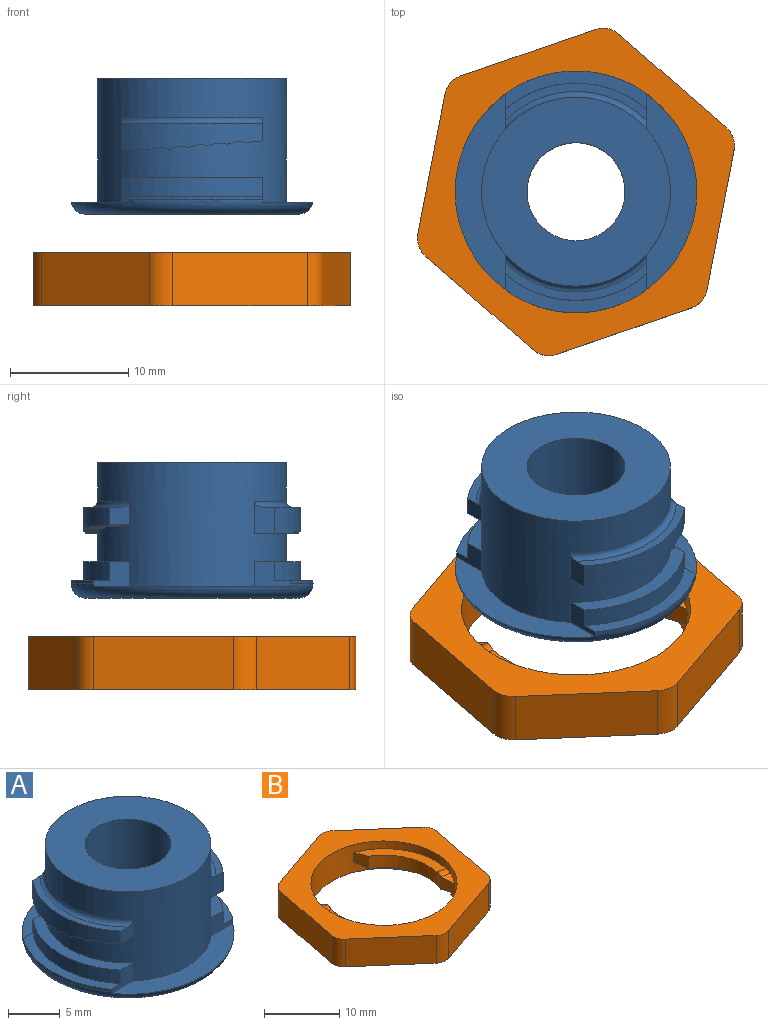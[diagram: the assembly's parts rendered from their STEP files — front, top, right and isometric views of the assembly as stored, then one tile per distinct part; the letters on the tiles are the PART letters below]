
ASSEMBLY  parts=2 mates=1
PART A: 51 faces, bbox 22.2x22.2x11.5 mm
  f0: plane 12x3.28mm, normal (0,0,1), area 13.6mm2, adj f1,f5,f6,f42
  f1: cylinder r=10.25mm len=12mm, axis (0,0,-1), area 3.8mm2, adj f0,f2,f5,f6
  f2: torus R=9.05mm, axis (0,0,-1), area 108.5mm2, adj f1,f3,f4,f5,f6,f37,f38,f49
  f3: plane 3.03x2.11mm, normal (0,1,0), area 4.2mm2, adj f2,f35,f36,f37,f43,f44,f50
  f4: plane 3.03x2.11mm, normal (0,-1,0), area 4.2mm2, adj f2,f35,f36,f37,f43,f44,f49
  f5: plane 3.03x2.11mm, normal (0,-1,0), area 4.2mm2, adj f0,f1,f2,f35,f42,f45,f49
  f6: plane 3.03x2.11mm, normal (0,1,0), area 4.2mm2, adj f0,f1,f2,f35,f42,f45,f50
  f7: plane 2.7x1.68mm, normal (0,1,0), area 3.8mm2, adj f8,f32,f35,f40,f46
  f8: plane 3.22x2.5mm, normal (0,0,-1), area 3.7mm2, adj f7,f34,f35,f40
  f9: plane 2.7x1.68mm, normal (0,-1,0), area 3.8mm2, adj f10,f20,f35,f41,f47
  f10: plane 3.22x2.5mm, normal (0,0,-1), area 3.7mm2, adj f9,f22,f35,f41
  f11: plane 2.7x1.43mm, normal (0,0.09,-1), area 2.2mm2, adj f12,f21,f35,f41
  f12: cylinder r=1.95mm len=2.11mm, axis (1,0,0), area 2mm2, adj f11,f13,f35,f41
  f13: plane 1.34x0.15mm, normal (0,0.09,-1), area 0.2mm2, adj f12,f14,f35,f41
  f14: cylinder r=1.95mm len=1.64mm, axis (1,0,0), area 1.9mm2, adj f13,f15,f35,f41
  f15: plane 1.24x0.15mm, normal (0,0.09,-1), area 0.2mm2, adj f14,f16,f35,f41
  f16: cylinder r=1.95mm len=1.49mm, axis (1,0,0), area 1.9mm2, adj f15,f17,f35,f41
  f17: plane 1.21x0.15mm, normal (0,0.09,-1), area 0.2mm2, adj f16,f18,f35,f41
  f18: cylinder r=1.95mm len=1.49mm, axis (1,0,0), area 1.9mm2, adj f17,f19,f35,f41
  f19: plane 1.27x0.15mm, normal (0,0.09,-1), area 0.2mm2, adj f18,f22,f35,f41
  f20: plane 12x3.18mm, normal (0,0,1), area 9.2mm2, adj f9,f21,f41,f47
  f21: plane 2x1.68mm, normal (0,1,0), area 2.6mm2, adj f11,f20,f35,f41,f47
  f22: cylinder r=1.95mm len=1.79mm, axis (1,0,0), area 2mm2, adj f10,f19,f35,f41
  f23: plane 2.7x1.43mm, normal (0,-0.09,-1), area 2.2mm2, adj f24,f33,f35,f40
  f24: cylinder r=1.95mm len=2.11mm, axis (-1,0,0), area 2mm2, adj f23,f25,f35,f40
  f25: plane 1.34x0.15mm, normal (0,-0.09,-1), area 0.2mm2, adj f24,f26,f35,f40
  f26: cylinder r=1.95mm len=1.64mm, axis (-1,0,0), area 1.9mm2, adj f25,f27,f35,f40
  f27: plane 1.24x0.15mm, normal (0,-0.09,-1), area 0.2mm2, adj f26,f28,f35,f40
  f28: cylinder r=1.95mm len=1.49mm, axis (-1,0,0), area 1.8mm2, adj f27,f29,f35,f40
  f29: plane 1.21x0.15mm, normal (0,-0.09,-1), area 0.2mm2, adj f28,f30,f35,f40
  f30: cylinder r=1.95mm len=1.49mm, axis (-1,0,0), area 1.9mm2, adj f29,f31,f35,f40
  f31: plane 1.27x0.15mm, normal (0,-0.09,-1), area 0.2mm2, adj f30,f34,f35,f40
  f32: plane 12x3.18mm, normal (0,0,1), area 9.2mm2, adj f7,f33,f40,f46
  f33: plane 2x1.68mm, normal (0,-1,0), area 2.6mm2, adj f23,f32,f35,f40,f46
  f34: cylinder r=1.95mm len=1.79mm, axis (-1,0,0), area 2mm2, adj f8,f31,f35,f40
  f35: cylinder r=8mm len=16mm, axis (0,0,-1), area 405.6mm2, adj f3,f4,f5,f6,f7,f8,f9,f10
  f36: plane 12x3.28mm, normal (0,0,1), area 13.6mm2, adj f3,f4,f37,f43
  f37: cylinder r=10.25mm len=12mm, axis (0,0,-1), area 3.8mm2, adj f2,f3,f4,f36
  f38: plane 18.1x18.1mm, normal (0,0,-1), area 203.2mm2, adj f2,f39
  f39: cylinder r=4.15mm len=11.5mm, axis (0,0,-1), area 299.9mm2, adj f38,f48
  f40: cylinder r=9.2mm len=12mm, axis (0,0,1), area 24.9mm2, adj f7,f8,f23,f24,f25,f26,f27,f28
  f41: cylinder r=9.2mm len=12mm, axis (0,0,1), area 24.9mm2, adj f9,f10,f11,f12,f13,f14,f15,f16
  f42: cylinder r=9.2mm len=12mm, axis (0,0,1), area 20.9mm2, adj f0,f5,f6,f45
  f43: cylinder r=9.2mm len=12mm, axis (0,0,1), area 20.9mm2, adj f3,f4,f36,f44
  f44: plane 12x3.91mm, normal (0,0,1), area 16mm2, adj f3,f4,f35,f43
  f45: plane 12x3.91mm, normal (0,0,1), area 16mm2, adj f5,f6,f35,f42
  f46: torus R=8.5mm, axis (0,0,-1), area 10.6mm2, adj f7,f32,f33,f35
  f47: torus R=8.5mm, axis (0,0,1), area 10.6mm2, adj f9,f20,f21,f35
  f48: plane 16x16mm, normal (0,0,1), area 147mm2, adj f35,f39
  f49: plane 16.58x4.23mm, normal (0,0,1), area 34.6mm2, adj f2,f4,f5,f35
  f50: plane 16.58x4.23mm, normal (0,0,1), area 34.6mm2, adj f2,f3,f6,f35
PART B: 33 faces, bbox 26.9x27.7x4.5 mm
  f0: cylinder r=1.28mm len=2.03mm, axis (0.66,0.75,0), area 1.9mm2, adj f1,f7,f8,f32
  f1: cylinder r=9.7mm len=19.4mm, axis (0,0,-1), area 207.6mm2, adj f0,f2,f3,f4,f5,f8,f9,f10
  f2: cylinder r=1.28mm len=2.03mm, axis (-0.66,-0.75,0), area 1.9mm2, adj f1,f5,f6,f31
  f3: plane 11.26x6.27mm, normal (0,0,1), area 18.4mm2, adj f1,f6,f11,f29
  f4: plane 11.26x6.27mm, normal (0,0,1), area 18.4mm2, adj f1,f7,f10,f27
  f5: plane 12.58x4.59mm, normal (0,0,-1), area 18.4mm2, adj f1,f2,f6,f9
  f6: cylinder r=8.2mm len=10.15mm, axis (0,0,-1), area 23.6mm2, adj f2,f3,f5,f9,f11,f29,f30
  f7: cylinder r=8.2mm len=10.15mm, axis (0,0,-1), area 23.6mm2, adj f0,f4,f8,f10,f12,f27
  f8: plane 12.58x4.59mm, normal (0,0,-1), area 18.4mm2, adj f0,f1,f7,f12
  f9: plane 2x1.98mm, normal (-0.95,-0.33,0), area 3.7mm2, adj f1,f5,f6,f30
  f10: plane 2x1.98mm, normal (0.95,0.33,0), area 3.7mm2, adj f1,f4,f7,f32
  f11: plane 2x1.98mm, normal (-0.95,-0.33,0), area 3.7mm2, adj f1,f3,f6,f31
  f12: plane 2x1.98mm, normal (0.95,0.33,0), area 3.7mm2, adj f1,f7,f8,f28
  f13: plane 11.43x4.5mm, normal (-0.33,0.95,0), area 54.4mm2, adj f19,f20,f25,f26
  f14: plane 9.13x7.93mm, normal (-0.66,-0.75,0), area 54.4mm2, adj f21,f22,f25,f26
  f15: plane 11.87x4.5mm, normal (0.98,-0.19,0), area 54.4mm2, adj f23,f24,f25,f26
  f16: plane 11.43x4.5mm, normal (0.33,-0.95,0), area 54.4mm2, adj f22,f23,f25,f26
  f17: plane 11.87x4.5mm, normal (-0.98,0.19,0), area 54.4mm2, adj f20,f21,f25,f26
  f18: plane 9.13x7.93mm, normal (0.66,0.75,0), area 54.4mm2, adj f19,f24,f25,f26
  f19: cylinder r=2mm len=4.5mm, axis (0,0,1), area 9.4mm2, adj f13,f18,f25,f26
  f20: cylinder r=2mm len=4.5mm, axis (0,0,1), area 9.4mm2, adj f13,f17,f25,f26
  f21: cylinder r=2mm len=4.5mm, axis (0,0,1), area 9.4mm2, adj f14,f17,f25,f26
  f22: cylinder r=2mm len=4.5mm, axis (0,0,1), area 9.4mm2, adj f14,f16,f25,f26
  f23: cylinder r=2mm len=4.5mm, axis (0,0,1), area 9.4mm2, adj f15,f16,f25,f26
  f24: cylinder r=2mm len=4.5mm, axis (0,0,1), area 9.4mm2, adj f15,f18,f25,f26
  f25: plane 27.74x26.86mm, normal (0,0,1), area 241.9mm2, adj f1,f13,f14,f15,f16,f17,f18,f19
  f26: plane 27.74x26.86mm, normal (0,0,-1), area 241.9mm2, adj f1,f13,f14,f15,f16,f17,f18,f19
  f27: cylinder r=1.28mm len=1.84mm, axis (0.98,-0.19,0), area 1.9mm2, adj f1,f4,f7,f28
  f28: plane 1.99x1.5mm, normal (0.05,0.26,0.96), area 1.5mm2, adj f1,f12,f27
  f29: cylinder r=1.26mm len=1.84mm, axis (-0.98,0.19,0), area 1.9mm2, adj f1,f3,f6,f30
  f30: plane 1.99x1.5mm, normal (-0.05,-0.26,0.96), area 1.5mm2, adj f1,f6,f9,f29
  f31: plane 1.99x1.69mm, normal (-0.2,0.17,-0.96), area 1.5mm2, adj f1,f2,f11
  f32: plane 1.99x1.69mm, normal (0.2,-0.17,-0.96), area 1.5mm2, adj f0,f1,f10
PLACE A rot(axis=(0,0,1),90deg) t=(-0.06,-0.25,-4.82)mm fixed
PLACE B rot(axis=(0,0,-1),180deg) t=(-0.06,-0.25,-14.82)mm
MATE cylindrical A.f1 <-> B.f1  axis (0,0,-1) through (-0.06,-0.25,5.18)mm
